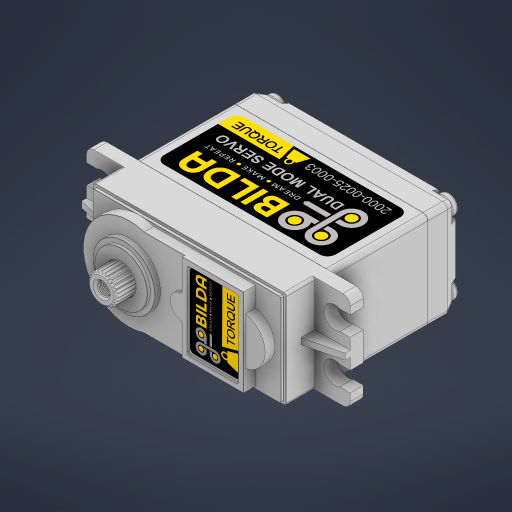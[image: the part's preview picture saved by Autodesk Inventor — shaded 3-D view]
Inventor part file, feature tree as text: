
AUTODESK INVENTOR PART (.ipt)
format: ipt  version: 2023 (Build 270158000, 158)  size: 1,654,784 bytes
history: native  units: in
note: dims shown in document units (in); Inventor stores cm internally (conversion verified against a paired STEP export)
features: other x6, sketch x2
ambient origin geometry x8: Origin, YZ Plane, XZ Plane, XY Plane, X Axis, Y Axis, Z Axis, Center Point
bodies: Solid1 (feature_tree), Solid2 (feature_tree)
feature tree (8):
  sketch  "Sketch1"
  sketch  "Sketch2"
  other  "Decal1"
  other  "Decal2"
  other  "Image3"
  other  "Image4"
  other  "Join1[1]"
  parser-record x1  (decoder bookkeeping rows leaked as tree rows — omitted from the tree; the rows remain in map.json)
